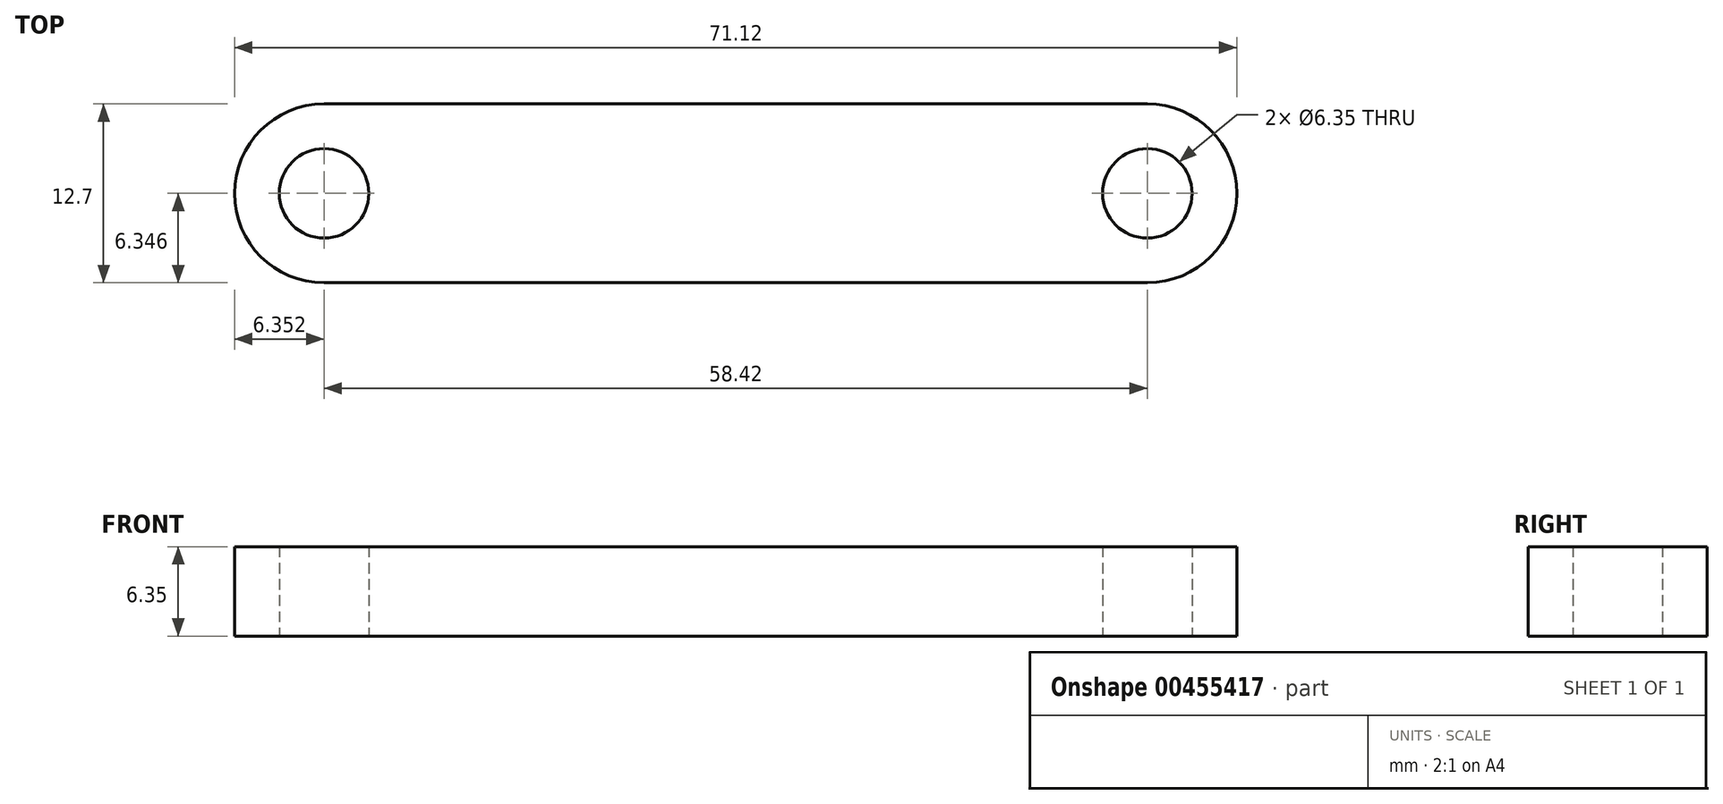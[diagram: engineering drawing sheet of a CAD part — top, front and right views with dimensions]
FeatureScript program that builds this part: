
annotation { "Feature Type Name" : "Feature", "Feature Type Description" : "" }
export const myFeature = defineFeature(function(context is Context, id is Id, definition is map)
    precondition{}
    {
        {
            var Q0;
            Q0=qCreatedBy(makeId("Top.planeOp"),FACE);
            var sketch = newSketch(context, id + "F0", { "sketchPlane" : qUnion([Q0])});
            skLineSegment(sketch, "E0.bottom", {"start": v(-4.33, -2.96) * mm, "end": v(54.1, -2.96) * mm});
            skLineSegment(sketch, "E0.top", {"start": v(-4.33, -15.66) * mm, "end": v(54.1, -15.66) * mm});
            skArc(sketch, "E1", {"start": v(-4.33, -2.96) * mm, "mid": v(-10.68, -9.31) * mm, "end": v(-4.33, -15.66) * mm});
            skArc(sketch, "E2", {"start": v(54.1, -15.66) * mm, "mid": v(60.44, -9.31) * mm, "end": v(54.1, -2.96) * mm});
            skCircle(sketch, "E3", {"center": v(-4.33, -9.31) * mm, "radius": 3.18 * mm});
            skCircle(sketch, "E4", {"center": v(54.1, -9.31) * mm, "radius": 3.18 * mm});
            skSolve(sketch);
        }
        {
            var Q0;
            Q0=makeQuery(id+"F0.imprint","IMPRINT",FACE,{"disambiguationData":[TD([[makeQuery(id+"F0.imprint","IMPRINT",EDGE,{"derivedFrom":sQuery(id+"F0.wireOp",EDGE,"E0.bottom")}),-1.0]])]});
            extrude(context, id + "F1", {"entities" : qUnion([Q0]), "depth" : 6.35 * mm});
        }
    });
